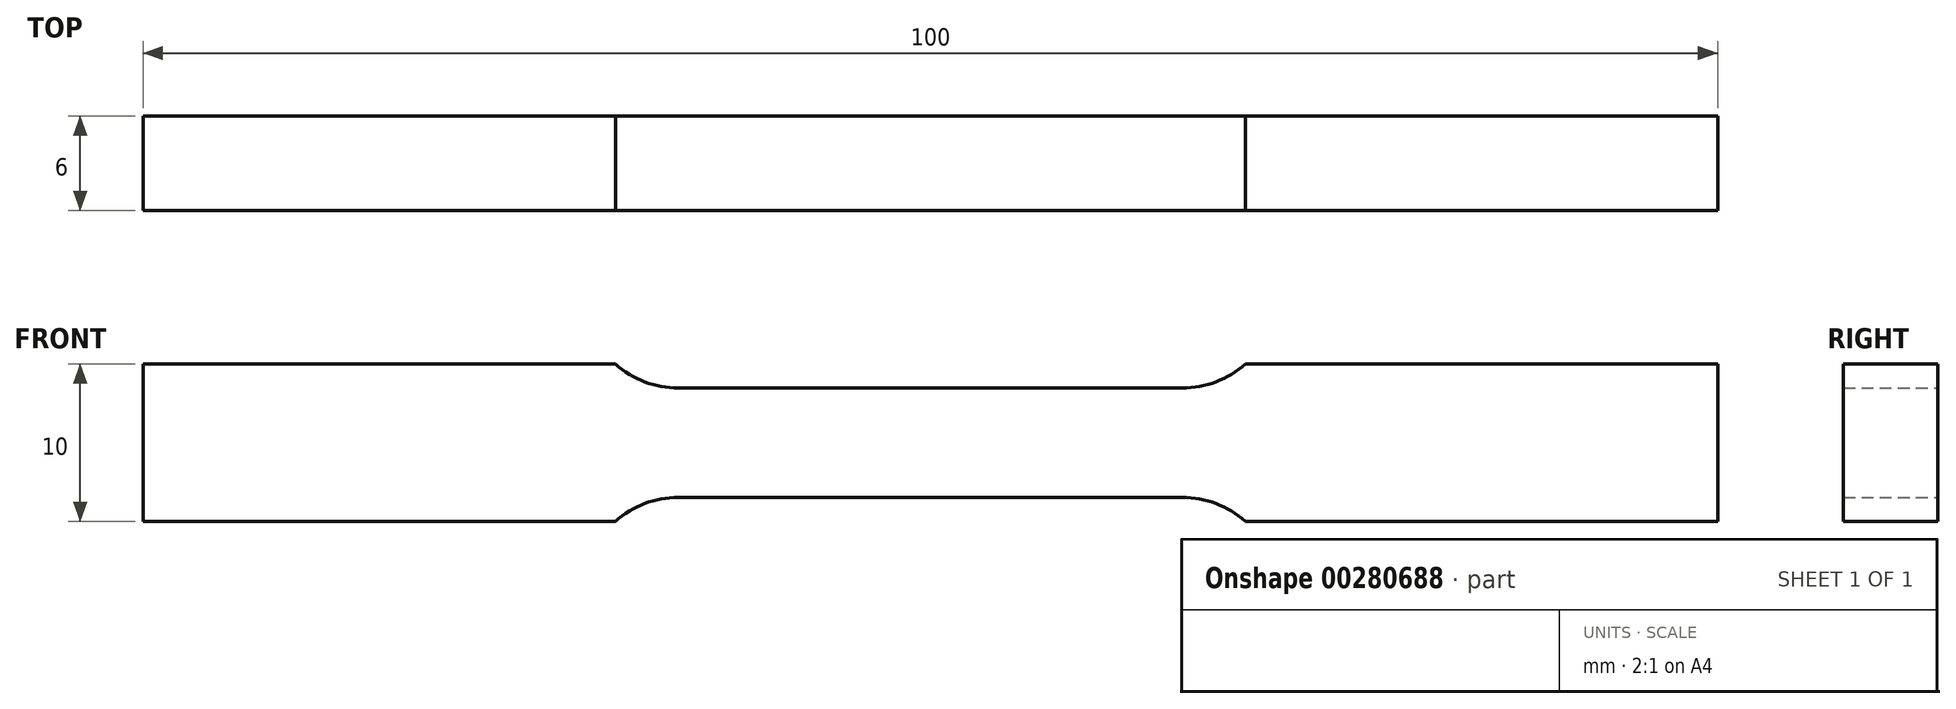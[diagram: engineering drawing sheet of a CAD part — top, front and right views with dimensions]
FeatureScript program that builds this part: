
annotation { "Feature Type Name" : "Feature", "Feature Type Description" : "" }
export const myFeature = defineFeature(function(context is Context, id is Id, definition is map)
    precondition{}
    {
        {
            var Q0;
            Q0=qCreatedBy(makeId("Front.planeOp"),FACE);
            var sketch = newSketch(context, id + "F0", { "sketchPlane" : qUnion([Q0])});
            skLineSegment(sketch, "E0", {"start": v(0, 3.47) * mm, "end": v(16, 3.47) * mm});
            skArc(sketch, "E1", {"start": v(16, 3.47) * mm, "mid": v(18.14, 3.87) * mm, "end": v(20, 5) * mm});
            skLineSegment(sketch, "E2", {"start": v(20, 5) * mm, "end": v(50, 5) * mm});
            skLineSegment(sketch, "E3", {"start": v(50, 5) * mm, "end": v(50, 0) * mm});
            skLineSegment(sketch, "E4.MirrorCS", {"start": v(0, -3.47) * mm, "end": v(16, -3.47) * mm});
            skLineSegment(sketch, "E5.MirrorCS", {"start": v(50, -5) * mm, "end": v(50, 0) * mm});
            skLineSegment(sketch, "E6.MirrorCS", {"start": v(20, -5) * mm, "end": v(50, -5) * mm});
            skArc(sketch, "E7.MirrorCS", {"start": v(16, -3.47) * mm, "mid": v(18.14, -3.87) * mm, "end": v(20, -5) * mm});
            skArc(sketch, "E8.MirrorCS", {"start": v(-16, -3.47) * mm, "mid": v(-18.14, -3.87) * mm, "end": v(-20, -5) * mm});
            skLineSegment(sketch, "E9.MirrorCS", {"start": v(-20, -5) * mm, "end": v(-50, -5) * mm});
            skArc(sketch, "E10.MirrorCS", {"start": v(-16, 3.47) * mm, "mid": v(-18.14, 3.87) * mm, "end": v(-20, 5) * mm});
            skLineSegment(sketch, "E11.MirrorCS", {"start": v(-20, 5) * mm, "end": v(-50, 5) * mm});
            skLineSegment(sketch, "E12.MirrorCS", {"start": v(-50, -5) * mm, "end": v(-50, 0) * mm});
            skLineSegment(sketch, "E13.MirrorCS", {"start": v(0, -3.47) * mm, "end": v(-16, -3.47) * mm});
            skLineSegment(sketch, "E14.MirrorCS", {"start": v(-50, 5) * mm, "end": v(-50, 0) * mm});
            skLineSegment(sketch, "E15.MirrorCS", {"start": v(0, 3.47) * mm, "end": v(-16, 3.47) * mm});
            skSolve(sketch);
        }
        {
            var Q0;
            Q0 = qSketchRegion(id + "F0", true);
            extrude(context, id + "F1", {"entities" : qUnion([Q0]), "endBound" : BoundingType.SYMMETRIC, "depth" : 6 * mm});
        }
    });
